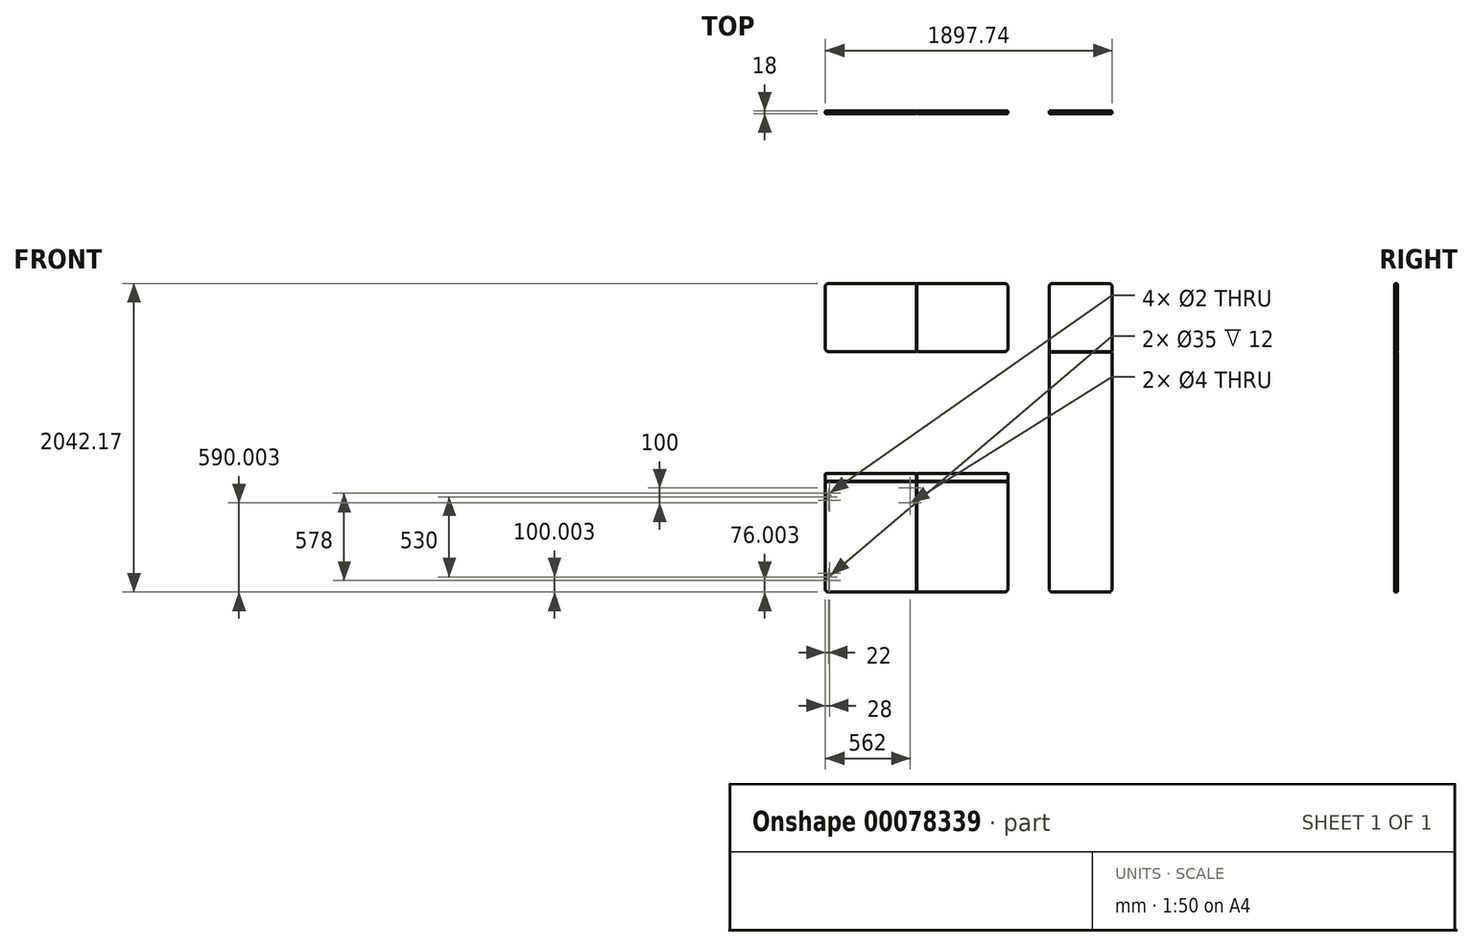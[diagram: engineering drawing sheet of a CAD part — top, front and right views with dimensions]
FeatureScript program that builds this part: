
annotation { "Feature Type Name" : "Feature", "Feature Type Description" : "" }
export const myFeature = defineFeature(function(context is Context, id is Id, definition is map)
    precondition{}
    {
        {
            var Q0;
            Q0=qCreatedBy(makeId("Front.planeOp"),FACE);
            var sketch = newSketch(context, id + "F0", { "sketchPlane" : qUnion([Q0])});
            skLineSegment(sketch, "E0.bottom", {"start": v(-303.1, 425.21) * mm, "end": v(298.9, 425.21) * mm});
            skLineSegment(sketch, "E0.top", {"start": v(-303.1, -304.79) * mm, "end": v(298.9, -304.79) * mm});
            skLineSegment(sketch, "E0.left", {"start": v(-303.1, 425.21) * mm, "end": v(-303.1, -304.79) * mm});
            skLineSegment(sketch, "E0.right", {"start": v(298.9, 425.21) * mm, "end": v(298.9, -304.79) * mm});
            skPoint(sketch, "E1.firstSnap0", {"position": v(-2.1, 425.21) * mm});
            skLineSegment(sketch, "E1.bottom", {"start": v(302.9, 425.21) * mm, "end": v(904.9, 425.21) * mm});
            skLineSegment(sketch, "E1.top", {"start": v(302.9, -304.79) * mm, "end": v(904.9, -304.79) * mm});
            skLineSegment(sketch, "E1.left", {"start": v(302.9, 425.21) * mm, "end": v(302.9, -304.79) * mm});
            skLineSegment(sketch, "E1.right", {"start": v(904.9, 425.21) * mm, "end": v(904.9, -304.79) * mm});
            skLineSegment(sketch, "E2.bottom", {"start": v(-303.1, 429.21) * mm, "end": v(298.9, 429.21) * mm});
            skLineSegment(sketch, "E2.top", {"start": v(-303.1, 479.21) * mm, "end": v(298.9, 479.21) * mm});
            skLineSegment(sketch, "E2.left", {"start": v(-303.1, 429.21) * mm, "end": v(-303.1, 479.21) * mm});
            skLineSegment(sketch, "E2.right", {"start": v(298.9, 429.21) * mm, "end": v(298.9, 479.21) * mm});
            skLineSegment(sketch, "E3.bottom", {"start": v(302.9, 429.21) * mm, "end": v(904.9, 429.21) * mm});
            skLineSegment(sketch, "E3.top", {"start": v(302.9, 479.21) * mm, "end": v(904.9, 479.21) * mm});
            skLineSegment(sketch, "E3.left", {"start": v(302.9, 429.21) * mm, "end": v(302.9, 479.21) * mm});
            skLineSegment(sketch, "E3.right", {"start": v(904.9, 429.21) * mm, "end": v(904.9, 479.21) * mm});
            skLineSegment(sketch, "E4.bottom", {"start": v(-303.1, 1287.38) * mm, "end": v(298.9, 1287.38) * mm});
            skLineSegment(sketch, "E4.top", {"start": v(-303.1, 1737.38) * mm, "end": v(298.9, 1737.38) * mm});
            skLineSegment(sketch, "E4.left", {"start": v(-303.1, 1287.38) * mm, "end": v(-303.1, 1737.38) * mm});
            skLineSegment(sketch, "E4.right", {"start": v(298.9, 1287.38) * mm, "end": v(298.9, 1737.38) * mm});
            skLineSegment(sketch, "E5.bottom", {"start": v(302.9, 1287.38) * mm, "end": v(904.9, 1287.38) * mm});
            skLineSegment(sketch, "E5.top", {"start": v(302.9, 1737.38) * mm, "end": v(904.9, 1737.38) * mm});
            skLineSegment(sketch, "E5.left", {"start": v(302.9, 1287.38) * mm, "end": v(302.9, 1737.38) * mm});
            skLineSegment(sketch, "E5.right", {"start": v(904.9, 1287.38) * mm, "end": v(904.9, 1737.38) * mm});
            skLineSegment(sketch, "E6.bottom", {"start": v(1178.64, -304.79) * mm, "end": v(1594.64, -304.79) * mm});
            skLineSegment(sketch, "E6.top", {"start": v(1178.64, 1283.38) * mm, "end": v(1594.64, 1283.38) * mm});
            skLineSegment(sketch, "E6.left", {"start": v(1178.64, -304.79) * mm, "end": v(1178.64, 1283.38) * mm});
            skLineSegment(sketch, "E6.right", {"start": v(1594.64, -304.79) * mm, "end": v(1594.64, 1283.38) * mm});
            skLineSegment(sketch, "E7.bottom", {"start": v(1178.64, 1287.38) * mm, "end": v(1594.64, 1287.38) * mm});
            skLineSegment(sketch, "E7.top", {"start": v(1178.64, 1737.38) * mm, "end": v(1594.64, 1737.38) * mm});
            skLineSegment(sketch, "E7.left", {"start": v(1178.64, 1287.38) * mm, "end": v(1178.64, 1737.38) * mm});
            skLineSegment(sketch, "E7.right", {"start": v(1594.64, 1287.38) * mm, "end": v(1594.64, 1737.38) * mm});
            skSolve(sketch);
        }
        {
            var Q0;
            Q0=makeQuery(id+"F0.imprint","IMPRINT",FACE,{"disambiguationData":[TD([[makeQuery(id+"F0.imprint","IMPRINT",EDGE,{"derivedFrom":sQuery(id+"F0.wireOp",EDGE,"E0.bottom")}),-1.0]])]});
            var Q1;
            Q1=makeQuery(id+"F0.imprint","IMPRINT",FACE,{"disambiguationData":[TD([[makeQuery(id+"F0.imprint","IMPRINT",EDGE,{"derivedFrom":sQuery(id+"F0.wireOp",EDGE,"E1.bottom")}),-1.0]])]});
            var Q2;
            Q2=makeQuery(id+"F0.imprint","IMPRINT",FACE,{"disambiguationData":[TD([[makeQuery(id+"F0.imprint","IMPRINT",EDGE,{"derivedFrom":sQuery(id+"F0.wireOp",EDGE,"E2.bottom")}),1.0]])]});
            var Q3;
            Q3=makeQuery(id+"F0.imprint","IMPRINT",FACE,{"disambiguationData":[TD([[makeQuery(id+"F0.imprint","IMPRINT",EDGE,{"derivedFrom":sQuery(id+"F0.wireOp",EDGE,"E3.bottom")}),1.0]])]});
            var Q4;
            Q4=makeQuery(id+"F0.imprint","IMPRINT",FACE,{"disambiguationData":[TD([[makeQuery(id+"F0.imprint","IMPRINT",EDGE,{"derivedFrom":sQuery(id+"F0.wireOp",EDGE,"E4.bottom")}),1.0]])]});
            var Q5;
            Q5=makeQuery(id+"F0.imprint","IMPRINT",FACE,{"disambiguationData":[TD([[makeQuery(id+"F0.imprint","IMPRINT",EDGE,{"derivedFrom":sQuery(id+"F0.wireOp",EDGE,"E5.bottom")}),1.0]])]});
            var Q6;
            Q6=makeQuery(id+"F0.imprint","IMPRINT",FACE,{"disambiguationData":[TD([[makeQuery(id+"F0.imprint","IMPRINT",EDGE,{"derivedFrom":sQuery(id+"F0.wireOp",EDGE,"E6.bottom")}),1.0]])]});
            var Q7;
            Q7=makeQuery(id+"F0.imprint","IMPRINT",FACE,{"disambiguationData":[TD([[makeQuery(id+"F0.imprint","IMPRINT",EDGE,{"derivedFrom":sQuery(id+"F0.wireOp",EDGE,"E7.bottom")}),1.0]])]});
            extrude(context, id + "F1", {"entities" : qUnion([Q0, Q1, Q2, Q3, Q4, Q5, Q6, Q7]), "depth" : 18 * mm, "offsetDistance" : 25 * mm});
        }
        {
            var Q0;
            Q0=makeQuery(id+"F1.opExtrude","CAP_FACE",FACE,{"disambiguationData":[OSD([sQuery(id+"F0.wireOp",EDGE,"E0.bottom"),sQuery(id+"F0.wireOp",EDGE,"E0.top"),sQuery(id+"F0.wireOp",EDGE,"E0.left"),sQuery(id+"F0.wireOp",EDGE,"E0.right")])],"isStart":true});
            var sketch = newSketch(context, id + "F2", { "sketchPlane" : qUnion([Q0])});
            skLineSegment(sketch, "E8", {"start": v(303.1, 325.21) * mm, "end": v(281.1, 325.21) * mm, "construction": true});
            skLineSegment(sketch, "E9", {"start": v(303.1, -204.79) * mm, "end": v(281.1, -204.79) * mm, "construction": true});
            skLineSegment(sketch, "E10", {"start": v(-258.9, 425.21) * mm, "end": v(-258.9, 385.21) * mm, "construction": true});
            skLineSegment(sketch, "E11", {"start": v(-258.9, 385.21) * mm, "end": v(-298.9, 385.21) * mm, "construction": true});
            skLineSegment(sketch, "E12", {"start": v(-258.9, 385.21) * mm, "end": v(-258.9, 285.21) * mm, "construction": true});
            skLineSegment(sketch, "E13", {"start": v(275.1, 349.21) * mm, "end": v(275.1, 301.21) * mm, "construction": true});
            skLineSegment(sketch, "E14", {"start": v(275.1, -180.79) * mm, "end": v(275.1, -228.79) * mm, "construction": true});
            skLineSegment(sketch, "E15", {"start": v(275.1, 325.21) * mm, "end": v(281.1, 325.21) * mm, "construction": true});
            skLineSegment(sketch, "E16", {"start": v(275.1, -204.79) * mm, "end": v(281.1, -204.79) * mm, "construction": true});
            skCircle(sketch, "E17", {"center": v(281.1, 325.21) * mm, "radius": 17.5 * mm});
            skCircle(sketch, "E18", {"center": v(281.1, -204.79) * mm, "radius": 17.5 * mm});
            skSolve(sketch);
        }
        {
            var Q0;
            Q0 = qSketchRegion(id + "F2", true);
            extrude(context, id + "F3", {"entities" : qUnion([Q0]), "operationType" : NewBodyOperationType.REMOVE, "oppositeDirection" : true, "depth" : 12 * mm, "offsetDistance" : 25 * mm});
        }
        {
            var Q0;
            Q0=sQuery(id+"F2.wireOp",VERTEX,"E13.start");
            var Q1;
            Q1=sQuery(id+"F2.wireOp",VERTEX,"E13.end");
            var Q2;
            Q2=sQuery(id+"F2.wireOp",VERTEX,"E14.start");
            var Q3;
            Q3=sQuery(id+"F2.wireOp",VERTEX,"E14.end");
            var Q4;
            Q4=makeQuery(id+"F1.opExtrude","SWEPT_BODY",BODY,{"disambiguationData":[OSD([sQuery(id+"F0.wireOp",EDGE,"E0.bottom"),sQuery(id+"F0.wireOp",EDGE,"E0.top"),sQuery(id+"F0.wireOp",EDGE,"E0.left"),sQuery(id+"F0.wireOp",EDGE,"E0.right")])]});
            hole(context, id + "F4", {"style" : HoleStyle.SIMPLE, "endStyle" : HoleEndStyle.BLIND, "holeDiameter" : 2 * mm, "majorDiameter" : 5 * mm, "holeDepth" : 5 * mm, "isTappedThrough" : true, "tappedDepth" : 12 * mm, "tapClearance" : 3, "locations" : qUnion([Q0, Q1, Q2, Q3]), "scope" : qUnion([Q4]), "startStyle" : HoleStartStyle.SKETCH});
        }
        {
            var Q0;
            Q0=sQuery(id+"F2.wireOp",VERTEX,"E11.start");
            var Q1;
            Q1=sQuery(id+"F2.wireOp",VERTEX,"E12.end");
            var Q2;
            Q2=makeQuery(id+"F1.opExtrude","SWEPT_BODY",BODY,{"disambiguationData":[OSD([sQuery(id+"F0.wireOp",EDGE,"E0.bottom"),sQuery(id+"F0.wireOp",EDGE,"E0.top"),sQuery(id+"F0.wireOp",EDGE,"E0.left"),sQuery(id+"F0.wireOp",EDGE,"E0.right")])]});
            hole(context, id + "F5", {"style" : HoleStyle.SIMPLE, "endStyle" : HoleEndStyle.THROUGH, "holeDiameter" : 4 * mm, "majorDiameter" : 5 * mm, "isTappedThrough" : true, "tappedDepth" : 12 * mm, "tapClearance" : 3, "locations" : qUnion([Q0, Q1]), "scope" : qUnion([Q2]), "startStyle" : HoleStartStyle.SKETCH});
        }
        {
            var Q0;
            Q0=makeQuery(id+"F1.opExtrude","SWEPT_EDGE",EDGE,{"disambiguationData":[OSD([sQuery(id+"F0.wireOp",EDGE,"E0.top"),sQuery(id+"F0.wireOp",EDGE,"E0.left")])]});
            var Q1;
            Q1=makeQuery(id+"F1.opExtrude","SWEPT_EDGE",EDGE,{"disambiguationData":[OSD([sQuery(id+"F0.wireOp",EDGE,"E1.top"),sQuery(id+"F0.wireOp",EDGE,"E1.right")])]});
            var Q2;
            Q2=makeQuery(id+"F1.opExtrude","SWEPT_EDGE",EDGE,{"disambiguationData":[OSD([sQuery(id+"F0.wireOp",EDGE,"E6.bottom"),sQuery(id+"F0.wireOp",EDGE,"E6.left")])]});
            var Q3;
            Q3=makeQuery(id+"F1.opExtrude","SWEPT_EDGE",EDGE,{"disambiguationData":[OSD([sQuery(id+"F0.wireOp",EDGE,"E6.bottom"),sQuery(id+"F0.wireOp",EDGE,"E6.right")])]});
            var Q4;
            Q4=makeQuery(id+"F1.opExtrude","SWEPT_EDGE",EDGE,{"disambiguationData":[OSD([sQuery(id+"F0.wireOp",EDGE,"E7.top"),sQuery(id+"F0.wireOp",EDGE,"E7.right")])]});
            var Q5;
            Q5=makeQuery(id+"F1.opExtrude","SWEPT_EDGE",EDGE,{"disambiguationData":[OSD([sQuery(id+"F0.wireOp",EDGE,"E7.top"),sQuery(id+"F0.wireOp",EDGE,"E7.left")])]});
            var Q6;
            Q6=makeQuery(id+"F1.opExtrude","SWEPT_EDGE",EDGE,{"disambiguationData":[OSD([sQuery(id+"F0.wireOp",EDGE,"E5.top"),sQuery(id+"F0.wireOp",EDGE,"E5.right")])]});
            var Q7;
            Q7=makeQuery(id+"F1.opExtrude","SWEPT_EDGE",EDGE,{"disambiguationData":[OSD([sQuery(id+"F0.wireOp",EDGE,"E4.top"),sQuery(id+"F0.wireOp",EDGE,"E4.left")])]});
            var Q8;
            Q8=makeQuery(id+"F1.opExtrude","SWEPT_EDGE",EDGE,{"disambiguationData":[OSD([sQuery(id+"F0.wireOp",EDGE,"E4.bottom"),sQuery(id+"F0.wireOp",EDGE,"E4.left")])]});
            var Q9;
            Q9=makeQuery(id+"F1.opExtrude","SWEPT_EDGE",EDGE,{"disambiguationData":[OSD([sQuery(id+"F0.wireOp",EDGE,"E5.bottom"),sQuery(id+"F0.wireOp",EDGE,"E5.right")])]});
            fillet(context, id + "F6", {"entities" : qUnion([Q0, Q1, Q2, Q3, Q4, Q5, Q6, Q7, Q8, Q9]), "radius" : 20 * mm, "tangentPropagation" : true, "allowEdgeOverflow" : false});
        }
        {
            var Q0;
            Q0=makeQuery(id+"F1.opExtrude","CAP_EDGE",EDGE,{"disambiguationData":[OSD([sQuery(id+"F0.wireOp",EDGE,"E0.top")])],"isStart":false});
            var Q1;
            Q1=makeQuery(id+"F1.opExtrude","CAP_EDGE",EDGE,{"disambiguationData":[OSD([sQuery(id+"F0.wireOp",EDGE,"E2.left")])],"isStart":false});
            var Q2;
            Q2=makeQuery(id+"F1.opExtrude","CAP_EDGE",EDGE,{"disambiguationData":[OSD([sQuery(id+"F0.wireOp",EDGE,"E1.top")])],"isStart":false});
            var Q3;
            Q3=makeQuery(id+"F1.opExtrude","CAP_EDGE",EDGE,{"disambiguationData":[OSD([sQuery(id+"F0.wireOp",EDGE,"E3.right")])],"isStart":false});
            var Q4;
            Q4=makeQuery(id+"F1.opExtrude","CAP_EDGE",EDGE,{"disambiguationData":[OSD([sQuery(id+"F0.wireOp",EDGE,"E4.bottom")])],"isStart":false});
            var Q5;
            Q5=makeQuery(id+"F1.opExtrude","CAP_EDGE",EDGE,{"disambiguationData":[OSD([sQuery(id+"F0.wireOp",EDGE,"E5.bottom")])],"isStart":false});
            var Q6;
            Q6=makeQuery(id+"F1.opExtrude","CAP_EDGE",EDGE,{"disambiguationData":[OSD([sQuery(id+"F0.wireOp",EDGE,"E7.left")])],"isStart":false});
            var Q7;
            Q7=makeQuery(id+"F1.opExtrude","CAP_EDGE",EDGE,{"disambiguationData":[OSD([sQuery(id+"F0.wireOp",EDGE,"E6.left")])],"isStart":false});
            fillet(context, id + "F7", {"entities" : qUnion([Q0, Q1, Q2, Q3, Q4, Q5, Q6, Q7]), "radius" : 6.5 * mm, "tangentPropagation" : true, "allowEdgeOverflow" : false});
        }
        {
            var Q0;
            Q0=makeQuery(id+"F1.opExtrude","SWEPT_EDGE",EDGE,{"disambiguationData":[OSD([sQuery(id+"F0.wireOp",EDGE,"E0.bottom"),sQuery(id+"F0.wireOp",EDGE,"E0.right")])]});
            var Q1;
            Q1=makeQuery(id+"F1.opExtrude","CAP_EDGE",EDGE,{"disambiguationData":[OSD([sQuery(id+"F0.wireOp",EDGE,"E0.bottom")])],"isStart":false});
            var Q2;
            Q2=makeQuery(id+"F1.opExtrude","CAP_EDGE",EDGE,{"disambiguationData":[OSD([sQuery(id+"F0.wireOp",EDGE,"E0.right")])],"isStart":false});
            var Q3;
            Q3=makeQuery(id+"F1.opExtrude","SWEPT_EDGE",EDGE,{"disambiguationData":[OSD([sQuery(id+"F0.wireOp",EDGE,"E1.bottom"),sQuery(id+"F0.wireOp",EDGE,"E1.left")])]});
            var Q4;
            Q4=makeQuery(id+"F1.opExtrude","CAP_EDGE",EDGE,{"disambiguationData":[OSD([sQuery(id+"F0.wireOp",EDGE,"E1.bottom")])],"isStart":false});
            var Q5;
            Q5=makeQuery(id+"F1.opExtrude","CAP_EDGE",EDGE,{"disambiguationData":[OSD([sQuery(id+"F0.wireOp",EDGE,"E1.left")])],"isStart":false});
            var Q6;
            Q6=makeQuery(id+"F1.opExtrude","SWEPT_EDGE",EDGE,{"disambiguationData":[OSD([sQuery(id+"F0.wireOp",EDGE,"E3.top"),sQuery(id+"F0.wireOp",EDGE,"E3.left")])]});
            var Q7;
            Q7=makeQuery(id+"F1.opExtrude","SWEPT_EDGE",EDGE,{"disambiguationData":[OSD([sQuery(id+"F0.wireOp",EDGE,"E2.top"),sQuery(id+"F0.wireOp",EDGE,"E2.right")])]});
            var Q8;
            Q8=makeQuery(id+"F1.opExtrude","SWEPT_EDGE",EDGE,{"disambiguationData":[OSD([sQuery(id+"F0.wireOp",EDGE,"E3.bottom"),sQuery(id+"F0.wireOp",EDGE,"E3.left")])]});
            var Q9;
            Q9=makeQuery(id+"F1.opExtrude","SWEPT_EDGE",EDGE,{"disambiguationData":[OSD([sQuery(id+"F0.wireOp",EDGE,"E2.bottom"),sQuery(id+"F0.wireOp",EDGE,"E2.right")])]});
            var Q10;
            Q10=makeQuery(id+"F1.opExtrude","CAP_EDGE",EDGE,{"disambiguationData":[OSD([sQuery(id+"F0.wireOp",EDGE,"E3.bottom")])],"isStart":false});
            var Q11;
            Q11=makeQuery(id+"F1.opExtrude","CAP_EDGE",EDGE,{"disambiguationData":[OSD([sQuery(id+"F0.wireOp",EDGE,"E3.left")])],"isStart":false});
            var Q12;
            Q12=makeQuery(id+"F1.opExtrude","CAP_EDGE",EDGE,{"disambiguationData":[OSD([sQuery(id+"F0.wireOp",EDGE,"E3.top")])],"isStart":false});
            var Q13;
            Q13=makeQuery(id+"F1.opExtrude","CAP_EDGE",EDGE,{"disambiguationData":[OSD([sQuery(id+"F0.wireOp",EDGE,"E2.bottom")])],"isStart":false});
            var Q14;
            Q14=makeQuery(id+"F1.opExtrude","CAP_EDGE",EDGE,{"disambiguationData":[OSD([sQuery(id+"F0.wireOp",EDGE,"E2.right")])],"isStart":false});
            var Q15;
            Q15=makeQuery(id+"F1.opExtrude","CAP_EDGE",EDGE,{"disambiguationData":[OSD([sQuery(id+"F0.wireOp",EDGE,"E2.top")])],"isStart":false});
            var Q16;
            Q16=makeQuery(id+"F1.opExtrude","CAP_EDGE",EDGE,{"disambiguationData":[OSD([sQuery(id+"F0.wireOp",EDGE,"E7.bottom")])],"isStart":false});
            var Q17;
            Q17=makeQuery(id+"F1.opExtrude","CAP_EDGE",EDGE,{"disambiguationData":[OSD([sQuery(id+"F0.wireOp",EDGE,"E6.top")])],"isStart":false});
            var Q18;
            Q18=makeQuery(id+"F1.opExtrude","CAP_EDGE",EDGE,{"disambiguationData":[OSD([sQuery(id+"F0.wireOp",EDGE,"E5.left")])],"isStart":false});
            var Q19;
            Q19=makeQuery(id+"F1.opExtrude","CAP_EDGE",EDGE,{"disambiguationData":[OSD([sQuery(id+"F0.wireOp",EDGE,"E4.right")])],"isStart":false});
            fillet(context, id + "F8", {"entities" : qUnion([Q0, Q1, Q2, Q3, Q4, Q5, Q6, Q7, Q8, Q9, Q10, Q11, Q12, Q13, Q14, Q15, Q16, Q17, Q18, Q19]), "radius" : 4 * mm, "tangentPropagation" : true, "allowEdgeOverflow" : false});
        }
        {
            var Q0;
            Q0=makeQuery(id+"F1.opExtrude","CAP_EDGE",EDGE,{"disambiguationData":[OSD([sQuery(id+"F0.wireOp",EDGE,"E0.bottom")])],"isStart":true});
            var Q1;
            Q1=makeQuery(id+"F1.opExtrude","CAP_EDGE",EDGE,{"disambiguationData":[OSD([sQuery(id+"F0.wireOp",EDGE,"E1.bottom")])],"isStart":true});
            var Q2;
            Q2=makeQuery(id+"F1.opExtrude","CAP_EDGE",EDGE,{"disambiguationData":[OSD([sQuery(id+"F0.wireOp",EDGE,"E3.bottom")])],"isStart":true});
            var Q3;
            Q3=makeQuery(id+"F1.opExtrude","CAP_EDGE",EDGE,{"disambiguationData":[OSD([sQuery(id+"F0.wireOp",EDGE,"E2.bottom")])],"isStart":true});
            var Q4;
            Q4=makeQuery(id+"F1.opExtrude","CAP_EDGE",EDGE,{"disambiguationData":[OSD([sQuery(id+"F0.wireOp",EDGE,"E4.bottom")])],"isStart":true});
            var Q5;
            Q5=makeQuery(id+"F1.opExtrude","CAP_EDGE",EDGE,{"disambiguationData":[OSD([sQuery(id+"F0.wireOp",EDGE,"E5.bottom")])],"isStart":true});
            var Q6;
            Q6=makeQuery(id+"F1.opExtrude","CAP_EDGE",EDGE,{"disambiguationData":[OSD([sQuery(id+"F0.wireOp",EDGE,"E6.top")])],"isStart":true});
            var Q7;
            Q7=makeQuery(id+"F1.opExtrude","CAP_EDGE",EDGE,{"disambiguationData":[OSD([sQuery(id+"F0.wireOp",EDGE,"E7.bottom")])],"isStart":true});
            fillet(context, id + "F9", {"entities" : qUnion([Q0, Q1, Q2, Q3, Q4, Q5, Q6, Q7]), "radius" : 4 * mm, "tangentPropagation" : true, "allowEdgeOverflow" : false});
        }
    });
